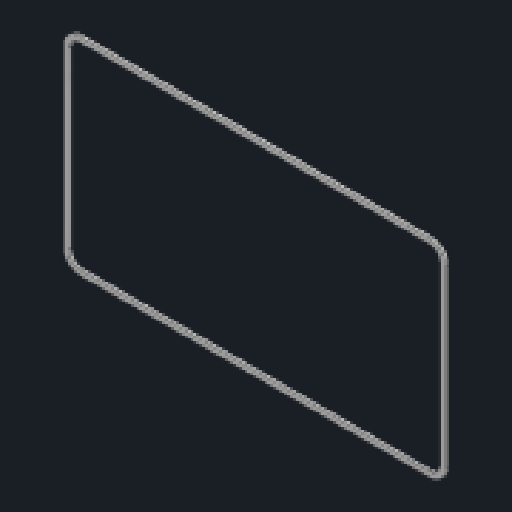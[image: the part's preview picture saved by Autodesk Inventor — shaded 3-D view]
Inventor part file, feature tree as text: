
AUTODESK INVENTOR PART (.ipt)
format: ipt  version: 2024 (Build 280153000, 153)  size: 99,328 bytes
history: native  units: in
note: dims shown in document units (in); Inventor stores cm internally (conversion verified against a paired STEP export)
features: other x3, extrude x1, sketch x1, reference x1
ambient origin geometry x8: Origin, YZ Plane, XZ Plane, XY Plane, X Axis, Y Axis, Z Axis, Center Point
bodies: Solid1 (feature_tree)
feature tree (6):
  extrude  "Extrusion1"  Depth=0.03in TaperAngle=0.0deg
  sketch  "Sketch1"  dims[d0=0.0625in d1=0.03in d2=0.0in]
  reference  "Reference1"
  parser-record x1  (decoder bookkeeping rows leaked as tree rows — omitted from the tree; the rows remain in map.json)
  other  "magplate.iam"
  other  "Part8"
note: 1 file-system path scrubbed to <path> (originals preserved in map.json)
